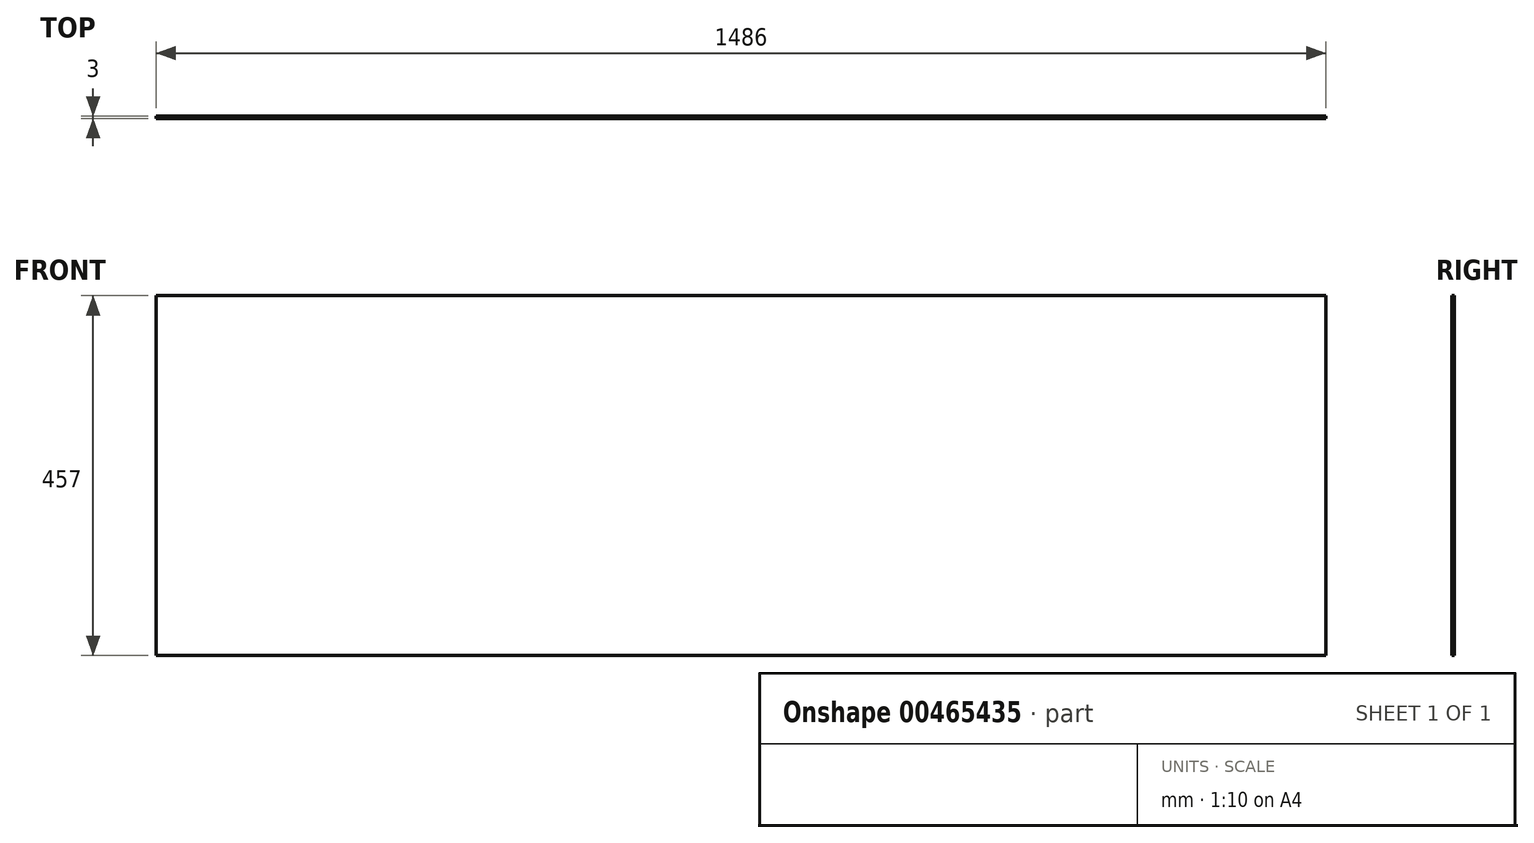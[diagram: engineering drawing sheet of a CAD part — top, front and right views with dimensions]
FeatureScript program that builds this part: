
annotation { "Feature Type Name" : "Feature", "Feature Type Description" : "" }
export const myFeature = defineFeature(function(context is Context, id is Id, definition is map)
    precondition{}
    {
        {
            var Q0;
            Q0=qCreatedBy(makeId("Front.planeOp"),FACE);
            var sketch = newSketch(context, id + "F0", { "sketchPlane" : qUnion([Q0])});
            skLineSegment(sketch, "E0.bottom", {"start": v(-745.65, -53.32) * mm, "end": v(740.35, -53.32) * mm});
            skLineSegment(sketch, "E0.top", {"start": v(-745.65, -510.32) * mm, "end": v(740.35, -510.32) * mm});
            skLineSegment(sketch, "E0.left", {"start": v(-745.65, -53.32) * mm, "end": v(-745.65, -510.32) * mm});
            skLineSegment(sketch, "E0.right", {"start": v(740.35, -53.32) * mm, "end": v(740.35, -510.32) * mm});
            skSolve(sketch);
        }
        {
            var Q0;
            Q0=makeQuery(id+"F0.imprint","IMPRINT",FACE,{"disambiguationData":[TD([[makeQuery(id+"F0.imprint","IMPRINT",EDGE,{"derivedFrom":sQuery(id+"F0.wireOp",EDGE,"E0.bottom")}),-1.0]])]});
            extrude(context, id + "F1", {"entities" : qUnion([Q0]), "depth" : 3 * mm, "offsetDistance" : 25 * mm});
        }
    });
